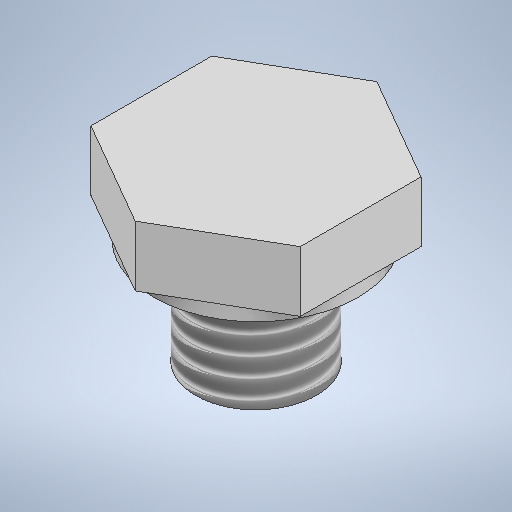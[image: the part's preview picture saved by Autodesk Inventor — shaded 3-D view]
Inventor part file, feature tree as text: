
AUTODESK INVENTOR PART (.ipt)
format: ipt  version: 2025.1 (Build 291241000, 241)  size: 279,040 bytes
history: native  units: mm
features: extrude x3, sketch x3, thread x1, other x1
ambient origin geometry x8: Origin, YZ Plane, XZ Plane, XY Plane, X Axis, Y Axis, Z Axis, Center Point
bodies: Solid1 (feature_tree)
feature tree (8):
  extrude  "Extrusion1"  Depth=4.0mm TaperAngle=0.0deg
  extrude  "Extrusion2"  Depth=8.0mm TaperAngle=0.0deg
  extrude  "Extrusion3"  Depth=8.0mm
  thread  "Thread1"  [1 undecoded]
  sketch  "Sketch1"  dims[d0=16.0mm d1=4.0mm d2=0.0mm]
  sketch  "Sketch2"  dims[d3=8.0mm d4=8.0mm d5=0.0mm]
  sketch  "Sketch3"  dims[d6=13.5mm d7=8.0mm d8=1.0mm d9=0.0mm d10=7.0mm d11=0.0mm]
  other  "Sicherung 122"
note: 1 required parameter value undecoded (feature->parameter linkage not recoverable at this tier; creation-order binding heuristic only, values carry confidence <= 0.55)
